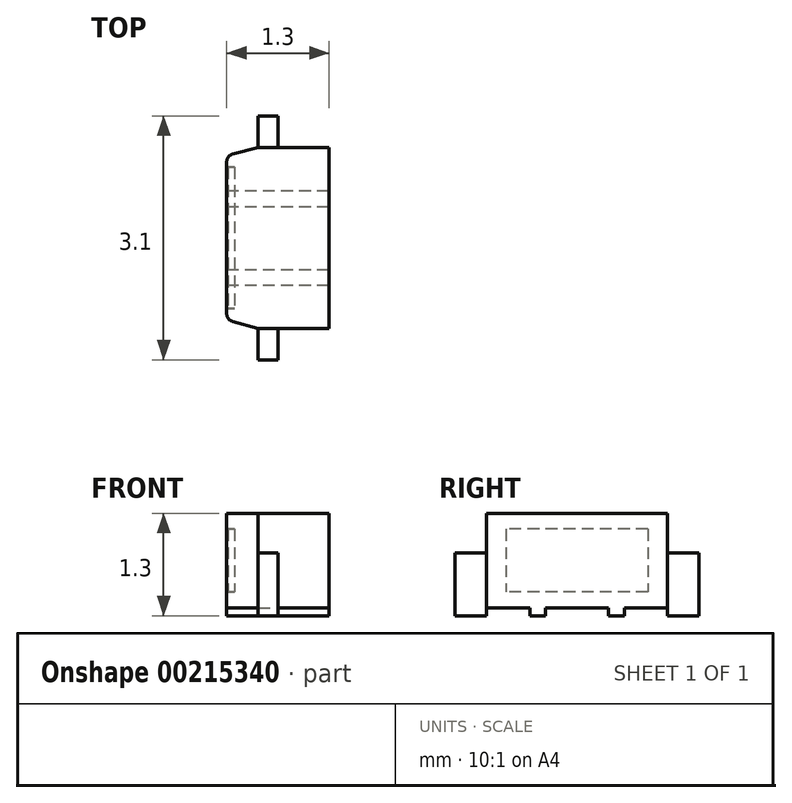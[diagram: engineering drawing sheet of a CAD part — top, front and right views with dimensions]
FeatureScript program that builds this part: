
annotation { "Feature Type Name" : "Feature", "Feature Type Description" : "" }
export const myFeature = defineFeature(function(context is Context, id is Id, definition is map)
    precondition{}
    {
        {
            var Q0;
            Q0=qCreatedBy(makeId("Top.planeOp"),FACE);
            var sketch = newSketch(context, id + "F0", { "sketchPlane" : qUnion([Q0])});
            skLineSegment(sketch, "E0.bottom", {"start": v(-0.25, 1.15) * mm, "end": v(0.65, 1.15) * mm});
            skLineSegment(sketch, "E0.top", {"start": v(-0.25, -1.15) * mm, "end": v(0.65, -1.15) * mm});
            skLineSegment(sketch, "E0.left", {"start": v(-0.65, 1.04) * mm, "end": v(-0.65, -1.04) * mm});
            skLineSegment(sketch, "E0.right", {"start": v(0.65, 1.15) * mm, "end": v(0.65, -1.15) * mm});
            skPoint(sketch, "E0.middle", {"position": v(0, 0) * mm});
            skLineSegment(sketch, "E1", {"start": v(-0.25, 1.15) * mm, "end": v(-0.65, 1.04) * mm});
            skLineSegment(sketch, "E2", {"start": v(-0.25, -1.15) * mm, "end": v(-0.65, -1.04) * mm});
            skPoint(sketch, "E3.orphan", {"position": v(-0.65, 1.15) * mm});
            skPoint(sketch, "E4.orphan", {"position": v(-0.65, -1.15) * mm});
            skSolve(sketch);
        }
        {
            var Q0;
            Q0 = qSketchRegion(id + "F0", true);
            extrude(context, id + "F1", {"entities" : qUnion([Q0]), "depth" : 1.2 * mm});
        }
        {
            var Q0;
            Q0=makeQuery(id+"F1.opExtrude","CAP_FACE",FACE,{"disambiguationData":[OSD([sQuery(id+"F0.wireOp",EDGE,"E0.bottom"),sQuery(id+"F0.wireOp",EDGE,"E0.top"),sQuery(id+"F0.wireOp",EDGE,"E0.left"),sQuery(id+"F0.wireOp",EDGE,"E0.right")])],"isStart":true});
            var sketch = newSketch(context, id + "F2", { "sketchPlane" : qUnion([Q0])});
            skLineSegment(sketch, "E5.bottom", {"start": v(-0.25, -1.55) * mm, "end": v(0, -1.55) * mm});
            skLineSegment(sketch, "E5.top", {"start": v(-0.25, 1.55) * mm, "end": v(0, 1.55) * mm});
            skLineSegment(sketch, "E5.left", {"start": v(-0.25, -1.55) * mm, "end": v(-0.25, -1.15) * mm});
            skLineSegment(sketch, "E5.right", {"start": v(0, -1.55) * mm, "end": v(0, -1.15) * mm});
            skPoint(sketch, "E5.middle", {"position": v(-0.12, 0) * mm});
            skLineSegment(sketch, "E6.bottom", {"start": v(-0.25, -1.15) * mm, "end": v(0, -1.15) * mm});
            skLineSegment(sketch, "E6.top", {"start": v(-0.25, 1.15) * mm, "end": v(0, 1.15) * mm});
            skLineSegment(sketch, "E7.trimOffspring", {"start": v(0, 1.15) * mm, "end": v(0, 1.55) * mm});
            skLineSegment(sketch, "E8.trimOffspring", {"start": v(-0.25, 1.15) * mm, "end": v(-0.25, 1.55) * mm});
            skSolve(sketch);
        }
        {
            var Q0;
            Q0 = qSketchRegion(id + "F2", true);
            extrude(context, id + "F3", {"entities" : qUnion([Q0]), "oppositeDirection" : true, "depth" : 0.7 * mm, "hasSecondDirection" : true, "secondDirectionOppositeDirection" : false, "secondDirectionDepth" : 0.1 * mm});
        }
        {
            var Q0;
            Q0=makeQuery(id+"F1.opExtrude","SWEPT_FACE",FACE,{"disambiguationData":[OSD([sQuery(id+"F0.wireOp",EDGE,"E0.left")])]});
            var sketch = newSketch(context, id + "F4", { "sketchPlane" : qUnion([Q0])});
            skLineSegment(sketch, "E9.bottom", {"start": v(-0.9, 1) * mm, "end": v(0.9, 1) * mm});
            skLineSegment(sketch, "E9.top", {"start": v(-0.9, 0.2) * mm, "end": v(0.9, 0.2) * mm});
            skLineSegment(sketch, "E9.left", {"start": v(-0.9, 1) * mm, "end": v(-0.9, 0.2) * mm});
            skLineSegment(sketch, "E9.right", {"start": v(0.9, 1) * mm, "end": v(0.9, 0.2) * mm});
            skPoint(sketch, "E9.middle", {"position": v(0, 0.6) * mm});
            skSolve(sketch);
        }
        {
            var Q0;
            Q0 = qSketchRegion(id + "F4", true);
            extrude(context, id + "F5", {"entities" : qUnion([Q0]), "operationType" : NewBodyOperationType.REMOVE, "oppositeDirection" : true, "depth" : 0.1 * mm});
        }
        {
            var Q0;
            Q0=makeQuery(id+"F5.boolean.opBoolean","COPY",FACE,{"derivedFrom":makeQuery(id+"F5.opExtrude","CAP_FACE",FACE,{"disambiguationData":[OSD([sQuery(id+"F4.wireOp",EDGE,"E9.bottom"),sQuery(id+"F4.wireOp",EDGE,"E9.top"),sQuery(id+"F4.wireOp",EDGE,"E9.left"),sQuery(id+"F4.wireOp",EDGE,"E9.right")])],"isStart":false})});
            var sketch = newSketch(context, id + "F6", { "sketchPlane" : qUnion([Q0])});
            skLineSegment(sketch, "E10.bottom", {"start": v(-0.9, 1) * mm, "end": v(0.9, 1) * mm});
            skLineSegment(sketch, "E10.top", {"start": v(-0.9, 0.2) * mm, "end": v(0.9, 0.2) * mm});
            skLineSegment(sketch, "E10.left", {"start": v(-0.9, 1) * mm, "end": v(-0.9, 0.2) * mm});
            skLineSegment(sketch, "E10.right", {"start": v(0.9, 1) * mm, "end": v(0.9, 0.2) * mm});
            skSolve(sketch);
        }
        {
            var Q0;
            Q0 = qSketchRegion(id + "F6", true);
            extrude(context, id + "F7", {"entities" : qUnion([Q0]), "depth" : 0.08 * mm});
        }
        {
            var Q0;
            Q0=makeQuery(id+"F1.opExtrude","SWEPT_EDGE",EDGE,{"disambiguationData":[OSD([sQuery(id+"F0.wireOp",EDGE,"E0.left"),sQuery(id+"F0.wireOp",EDGE,"E2")])]});
            var Q1;
            Q1=makeQuery(id+"F1.opExtrude","SWEPT_EDGE",EDGE,{"disambiguationData":[OSD([sQuery(id+"F0.wireOp",EDGE,"E0.left"),sQuery(id+"F0.wireOp",EDGE,"E1")])]});
            fillet(context, id + "F8", {"entities" : qUnion([Q0, Q1]), "radius" : 0.1 * mm, "tangentPropagation" : true, "allowEdgeOverflow" : false});
        }
        {
            var Q0;
            Q0=makeQuery(id+"F1.opExtrude","CAP_FACE",FACE,{"disambiguationData":[OSD([sQuery(id+"F0.wireOp",EDGE,"E0.bottom"),sQuery(id+"F0.wireOp",EDGE,"E0.top"),sQuery(id+"F0.wireOp",EDGE,"E0.left"),sQuery(id+"F0.wireOp",EDGE,"E0.right"),sQuery(id+"F0.wireOp",EDGE,"E1"),sQuery(id+"F0.wireOp",EDGE,"E2")])],"isStart":true});
            var sketch = newSketch(context, id + "F9", { "sketchPlane" : qUnion([Q0])});
            skLineSegment(sketch, "E11.bottom", {"start": v(-0.65, 0.6) * mm, "end": v(0.65, 0.6) * mm});
            skLineSegment(sketch, "E11.top", {"start": v(-0.65, 0.4) * mm, "end": v(0.65, 0.4) * mm});
            skLineSegment(sketch, "E11.left", {"start": v(-0.65, 0.6) * mm, "end": v(-0.65, 0.4) * mm});
            skLineSegment(sketch, "E11.right", {"start": v(0.65, 0.6) * mm, "end": v(0.65, 0.4) * mm});
            skLineSegment(sketch, "E12.bottom", {"start": v(-0.65, -0.4) * mm, "end": v(0.65, -0.4) * mm});
            skLineSegment(sketch, "E12.top", {"start": v(-0.65, -0.6) * mm, "end": v(0.65, -0.6) * mm});
            skLineSegment(sketch, "E12.left", {"start": v(-0.65, -0.4) * mm, "end": v(-0.65, -0.6) * mm});
            skLineSegment(sketch, "E12.right", {"start": v(0.65, -0.4) * mm, "end": v(0.65, -0.6) * mm});
            skSolve(sketch);
        }
        {
            var Q0;
            Q0 = qSketchRegion(id + "F9", true);
            extrude(context, id + "F10", {"entities" : qUnion([Q0]), "operationType" : NewBodyOperationType.ADD, "depth" : 0.1 * mm});
        }
    });
